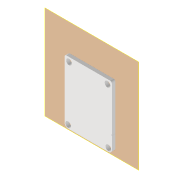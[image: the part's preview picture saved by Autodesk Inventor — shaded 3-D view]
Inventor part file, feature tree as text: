
AUTODESK INVENTOR PART (.ipt)
format: ipt  version: 2022 (Build 260153000, 153)  size: 138,240 bytes
history: native  units: mm
features: reference x8, sketch x3, other x3, plane x2, hole x2, projected_geometry x2, extrude x1, fillet x1
ambient origin geometry x8: Origin, YZ Plane, XZ Plane, XY Plane, X Axis, Y Axis, Z Axis, Center Point
bodies: Volumenkörper1 (feature_tree)
feature tree (22):
  plane  "Arbeitsebene1"
  extrude  "Extrusion1"  Depth=2.0mm
  plane  "Arbeitsebene2"
  hole  "Bohrung1"  [1 undecoded]
  fillet  "Rundung1"  [1 undecoded]
  hole  "Bohrung2"  [1 undecoded]
  sketch  "Skizze1"  dims[d2=2.0mm d3=0.0mm]
  reference  "Referenz1"
  sketch  "Skizze2"  dims[d4=3.2mm d5=6.0mm d6=4.0mm d7=2.0mm d8=90.0deg d9=8.0mm d10=20.594885mm d11=2.0mm]
  projected_geometry  "Projizierte Kontur1"
  reference  "Referenz2"
  reference  "Referenz3"
  reference  "Referenz4"
  reference  "Referenz5"
  reference  "Referenz6"
  reference  "Referenz7"
  reference  "Referenz8"
  sketch  "Skizze3"  dims[d13=2.5mm d14=3.2mm d15=6.0mm d16=6.5mm d17=3.0mm d18=90.0deg d19=8.0mm d20=20.594885mm]
  projected_geometry  "Projizierte Kontur2"
  other  "Assembly_Cube_SEEED_Xiao_Sense_Camera_v3.iam"
  other  "00_ESP32_XIAO_Adapter_base:1"
  other  "20_Cube_Insert_SEEED_Xiao_Sense_Camera:1"
note: 3 required parameter values undecoded (feature->parameter linkage not recoverable at this tier; creation-order binding heuristic only, values carry confidence <= 0.55)
